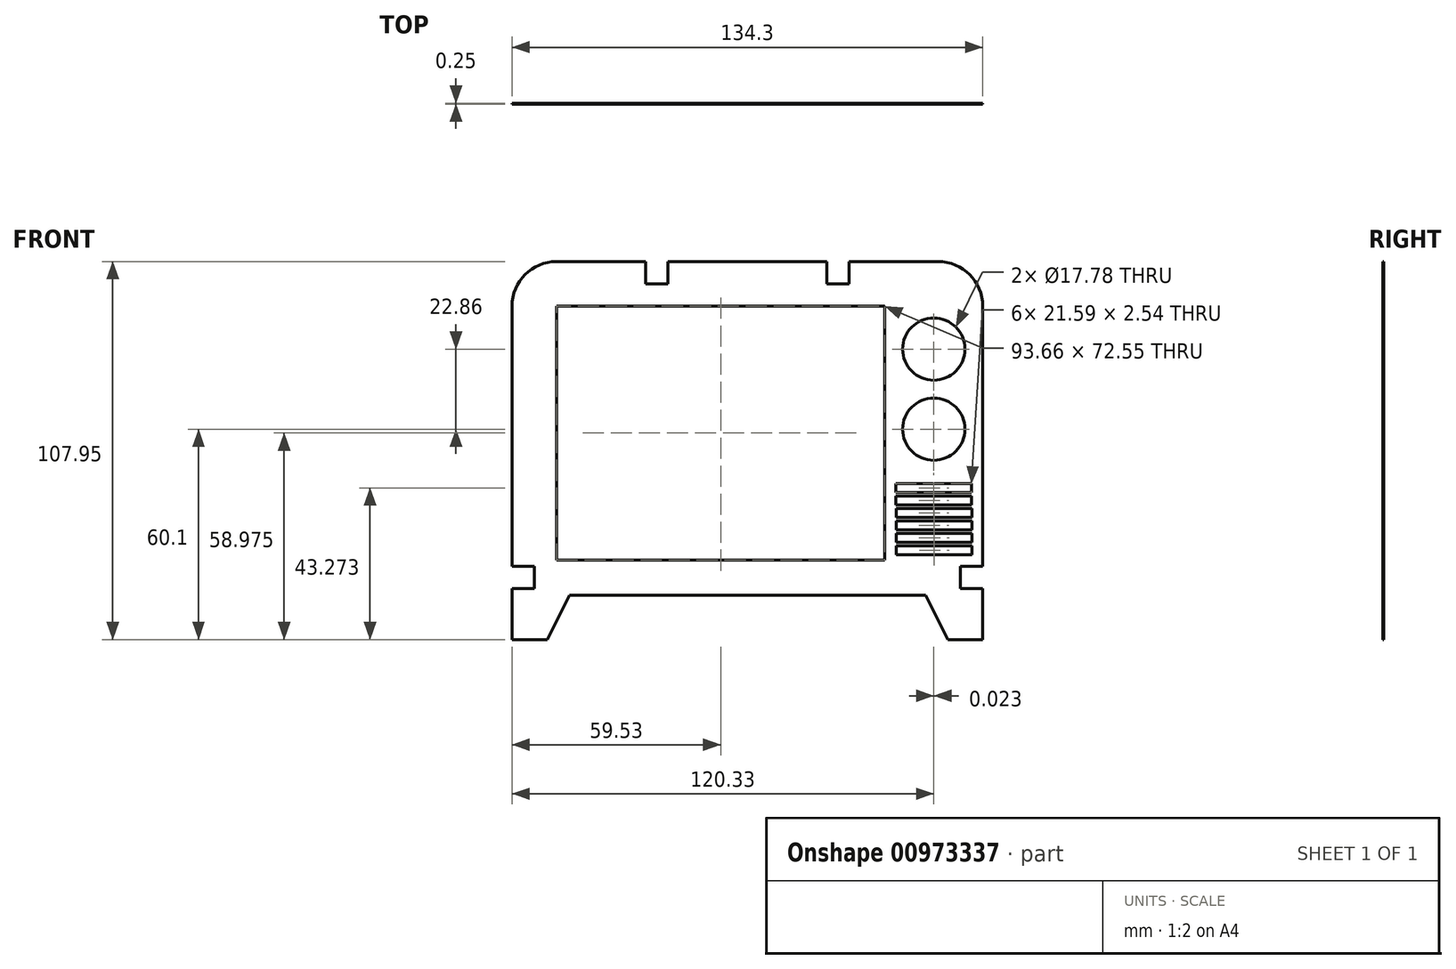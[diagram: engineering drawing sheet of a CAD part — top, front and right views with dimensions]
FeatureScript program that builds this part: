
annotation { "Feature Type Name" : "Feature", "Feature Type Description" : "" }
export const myFeature = defineFeature(function(context is Context, id is Id, definition is map)
    precondition{}
    {
        {
            assignVariable(context, id + "F0", {"name" : "Thick", "anyValue" : 0.25});
        }
        {
            var Q0;
            Q0=qCreatedBy(makeId("Front.planeOp"),FACE);
            var sketch = newSketch(context, id + "F1", { "sketchPlane" : qUnion([Q0])});
            skLineSegment(sketch, "E0", {"start": v(0, 0) * mm, "end": v(-50.8, 0) * mm});
            skLineSegment(sketch, "E1", {"start": v(-50.8, 0) * mm, "end": v(-57.15, -12.7) * mm});
            skLineSegment(sketch, "E2", {"start": v(-57.15, -12.7) * mm, "end": v(-67.15, -12.7) * mm});
            skLineSegment(sketch, "E3", {"start": v(0, 0) * mm, "end": v(0, 95.25) * mm, "construction": true});
            skLineSegment(sketch, "E4", {"start": v(0, 0) * mm, "end": v(-57.15, 0) * mm, "construction": true});
            skLineSegment(sketch, "E5", {"start": v(-57.15, 0) * mm, "end": v(-57.15, -12.7) * mm, "construction": true});
            skLineSegment(sketch, "E6.MirrorCS", {"start": v(0, 0) * mm, "end": v(50.8, 0) * mm});
            skLineSegment(sketch, "E7.MirrorCS", {"start": v(0, 0) * mm, "end": v(57.15, 0) * mm, "construction": true});
            skLineSegment(sketch, "E8.MirrorCS", {"start": v(57.15, 0) * mm, "end": v(57.15, -12.7) * mm, "construction": true});
            skLineSegment(sketch, "E9.MirrorCS", {"start": v(57.15, -12.7) * mm, "end": v(67.15, -12.7) * mm});
            skLineSegment(sketch, "E10.MirrorCS", {"start": v(50.8, 0) * mm, "end": v(57.15, -12.7) * mm});
            skPoint(sketch, "E11.visualSharp", {"position": v(-67.15, 95.25) * mm});
            skPoint(sketch, "E12.visualSharp", {"position": v(67.15, 95.25) * mm});
            skArc(sketch, "E12.filletArc", {"start": v(67.15, 82.55) * mm, "mid": v(63.43, 91.53) * mm, "end": v(54.45, 95.25) * mm});
            skLineSegment(sketch, "E13", {"start": v(-54.45, 82.55) * mm, "end": v(-54.45, 10) * mm});
            skLineSegment(sketch, "E14", {"start": v(-54.45, 10) * mm, "end": v(0, 10) * mm});
            skLineSegment(sketch, "E15", {"start": v(-54.45, 82.55) * mm, "end": v(0, 82.55) * mm});
            skLineSegment(sketch, "E16", {"start": v(0, 82.55) * mm, "end": v(39.2, 82.55) * mm});
            skLineSegment(sketch, "E17", {"start": v(0, 10) * mm, "end": v(39.21, 10) * mm});
            skLineSegment(sketch, "E18", {"start": v(39.2, 82.55) * mm, "end": v(39.21, 10) * mm});
            skLineSegment(sketch, "E19", {"start": v(67.15, 0) * mm, "end": v(53.18, 0) * mm, "construction": true});
            skLineSegment(sketch, "E20", {"start": v(53.18, -0.82) * mm, "end": v(53.18, 99.14) * mm, "construction": true});
            skLineSegment(sketch, "E21", {"start": v(84.24, 82.55) * mm, "end": v(84.24, 10) * mm, "construction": true});
            skCircle(sketch, "E22", {"center": v(53.18, 70.26) * mm, "radius": 8.9 * mm, "construction": true});
            skCircle(sketch, "E23.1.0.0", {"center": v(53.18, 47.4) * mm, "radius": 8.9 * mm, "construction": true});
            skLineSegment(sketch, "E23.direction1", {"start": v(53.18, 70.26) * mm, "end": v(53.18, 47.4) * mm, "construction": true});
            skLineSegment(sketch, "E24", {"start": v(63.18, 84.23) * mm, "end": v(63.18, 33.43) * mm, "construction": true});
            skLineSegment(sketch, "E25", {"start": v(63.18, 84.23) * mm, "end": v(36.84, 84.23) * mm, "construction": true});
            skLineSegment(sketch, "E26", {"start": v(63.18, 33.43) * mm, "end": v(34.94, 33.43) * mm, "construction": true});
            skLineSegment(sketch, "E27", {"start": v(63.18, 58.83) * mm, "end": v(36.84, 58.83) * mm, "construction": true});
            skLineSegment(sketch, "E28", {"start": v(53.18, 47.4) * mm, "end": v(53.18, 58.83) * mm, "construction": true});
            skLineSegment(sketch, "E29", {"start": v(53.18, 79.15) * mm, "end": v(53.18, 84.23) * mm, "construction": true});
            skLineSegment(sketch, "E30", {"start": v(53.18, 38.51) * mm, "end": v(53.18, 33.43) * mm, "construction": true});
            skLineSegment(sketch, "E31", {"start": v(53.18, 61.37) * mm, "end": v(53.18, 56.3) * mm, "construction": true});
            skCircle(sketch, "E32", {"center": v(53.18, 70.26) * mm, "radius": 8.9 * mm});
            skCircle(sketch, "E33", {"center": v(53.18, 47.4) * mm, "radius": 8.9 * mm});
            skLineSegment(sketch, "E34.bottom", {"start": v(42.38, 31.84) * mm, "end": v(63.98, 31.84) * mm});
            skLineSegment(sketch, "E34.top", {"start": v(42.38, 29.3) * mm, "end": v(63.98, 29.3) * mm});
            skLineSegment(sketch, "E34.left", {"start": v(42.38, 31.84) * mm, "end": v(42.38, 29.3) * mm});
            skLineSegment(sketch, "E34.right", {"start": v(63.98, 31.84) * mm, "end": v(63.98, 29.3) * mm});
            skLineSegment(sketch, "E35.1.0.0", {"start": v(42.4, 28.29) * mm, "end": v(42.4, 25.75) * mm});
            skLineSegment(sketch, "E35.1.0.1", {"start": v(42.4, 28.29) * mm, "end": v(64, 28.29) * mm});
            skLineSegment(sketch, "E35.1.0.2", {"start": v(42.4, 25.75) * mm, "end": v(64, 25.75) * mm});
            skLineSegment(sketch, "E35.1.0.3", {"start": v(64, 28.29) * mm, "end": v(64, 25.75) * mm});
            skLineSegment(sketch, "E35.2.0.0", {"start": v(42.43, 24.73) * mm, "end": v(42.43, 22.2) * mm});
            skLineSegment(sketch, "E35.2.0.1", {"start": v(42.43, 24.73) * mm, "end": v(64.02, 24.73) * mm});
            skLineSegment(sketch, "E35.2.0.2", {"start": v(42.43, 22.2) * mm, "end": v(64.02, 22.2) * mm});
            skLineSegment(sketch, "E35.2.0.3", {"start": v(64.02, 24.73) * mm, "end": v(64.02, 22.2) * mm});
            skLineSegment(sketch, "E35.direction1", {"start": v(42.38, 29.3) * mm, "end": v(42.4, 25.75) * mm, "construction": true});
            skLineSegment(sketch, "E36.0.3.0", {"start": v(42.45, 21.18) * mm, "end": v(42.45, 18.64) * mm});
            skLineSegment(sketch, "E36.3.3.0", {"start": v(42.45, 21.18) * mm, "end": v(64.04, 21.18) * mm});
            skLineSegment(sketch, "E36.6.3.0", {"start": v(42.45, 18.64) * mm, "end": v(64.04, 18.64) * mm});
            skLineSegment(sketch, "E36.9.3.0", {"start": v(64.04, 21.18) * mm, "end": v(64.04, 18.64) * mm});
            skLineSegment(sketch, "E36.0.4.0", {"start": v(42.48, 17.62) * mm, "end": v(42.48, 15.08) * mm});
            skLineSegment(sketch, "E36.3.4.0", {"start": v(42.48, 17.62) * mm, "end": v(64.07, 17.62) * mm});
            skLineSegment(sketch, "E36.6.4.0", {"start": v(42.48, 15.08) * mm, "end": v(64.07, 15.08) * mm});
            skLineSegment(sketch, "E36.9.4.0", {"start": v(64.07, 17.62) * mm, "end": v(64.07, 15.08) * mm});
            skLineSegment(sketch, "E37", {"start": v(-67.15, 70.65) * mm, "end": v(-67.15, 8.17) * mm});
            skLineSegment(sketch, "E38", {"start": v(-67.15, 8.17) * mm, "end": v(-60.8, 8.17) * mm});
            skLineSegment(sketch, "E39", {"start": v(-60.8, 8.17) * mm, "end": v(-60.8, 1.82) * mm});
            skLineSegment(sketch, "E40", {"start": v(-60.8, 1.82) * mm, "end": v(-67.15, 1.82) * mm});
            skLineSegment(sketch, "E41", {"start": v(-67.15, 1.82) * mm, "end": v(-67.15, -12.7) * mm});
            skLineSegment(sketch, "E42", {"start": v(-50.8, 0) * mm, "end": v(-50.8, 10) * mm, "construction": true});
            skPoint(sketch, "E43", {"position": v(-50.8, 5) * mm});
            skPoint(sketch, "E44", {"position": v(-60.8, 5) * mm});
            skLineSegment(sketch, "E45", {"start": v(-67.15, 70.65) * mm, "end": v(-67.15, 82.55) * mm});
            skLineSegment(sketch, "E46", {"start": v(-48.12, 95.25) * mm, "end": v(-54.45, 95.25) * mm});
            skArc(sketch, "E47.filletArc", {"start": v(-54.45, 95.25) * mm, "mid": v(-63.43, 91.53) * mm, "end": v(-67.15, 82.55) * mm});
            skLineSegment(sketch, "E48.MirrorCS", {"start": v(67.15, 8.17) * mm, "end": v(60.8, 8.17) * mm});
            skLineSegment(sketch, "E49.MirrorCS", {"start": v(60.8, 1.82) * mm, "end": v(67.15, 1.82) * mm});
            skLineSegment(sketch, "E50.MirrorCS", {"start": v(67.15, 1.82) * mm, "end": v(67.15, -12.7) * mm});
            skLineSegment(sketch, "E51.MirrorCS", {"start": v(60.8, 8.17) * mm, "end": v(60.8, 1.82) * mm});
            skPoint(sketch, "E52.MirrorP", {"position": v(60.8, 5) * mm});
            skLineSegment(sketch, "E53", {"start": v(67.15, 8.17) * mm, "end": v(67.15, 82.55) * mm});
            skLineSegment(sketch, "E54.0.5.0", {"start": v(42.5, 14.06) * mm, "end": v(42.5, 11.52) * mm});
            skLineSegment(sketch, "E54.3.5.0", {"start": v(42.5, 14.06) * mm, "end": v(64.09, 14.06) * mm});
            skLineSegment(sketch, "E54.6.5.0", {"start": v(42.5, 11.52) * mm, "end": v(64.09, 11.52) * mm});
            skLineSegment(sketch, "E54.9.5.0", {"start": v(64.09, 14.06) * mm, "end": v(64.09, 11.52) * mm});
            skLineSegment(sketch, "E55", {"start": v(-54.45, 95.25) * mm, "end": v(-29.05, 95.25) * mm, "construction": true});
            skLineSegment(sketch, "E56", {"start": v(-48.12, 95.25) * mm, "end": v(-29.05, 95.25) * mm});
            skLineSegment(sketch, "E57", {"start": v(-29.05, 88.9) * mm, "end": v(-22.7, 88.9) * mm});
            skLineSegment(sketch, "E58", {"start": v(-22.7, 88.9) * mm, "end": v(-22.7, 95.25) * mm});
            skLineSegment(sketch, "E59", {"start": v(-22.7, 95.25) * mm, "end": v(0, 95.25) * mm});
            skLineSegment(sketch, "E60", {"start": v(-29.05, 88.9) * mm, "end": v(-29.05, 95.25) * mm});
            skLineSegment(sketch, "E61.MirrorCS", {"start": v(48.12, 95.25) * mm, "end": v(54.45, 95.25) * mm});
            skLineSegment(sketch, "E62.MirrorCS", {"start": v(48.12, 95.25) * mm, "end": v(29.05, 95.25) * mm});
            skLineSegment(sketch, "E63.MirrorCS", {"start": v(22.7, 95.25) * mm, "end": v(0, 95.25) * mm});
            skLineSegment(sketch, "E64.MirrorCS", {"start": v(29.05, 88.9) * mm, "end": v(29.05, 95.25) * mm});
            skLineSegment(sketch, "E65.MirrorCS", {"start": v(22.7, 88.9) * mm, "end": v(22.7, 95.25) * mm});
            skLineSegment(sketch, "E66.MirrorCS", {"start": v(29.05, 88.9) * mm, "end": v(22.7, 88.9) * mm});
            skSolve(sketch);
        }
        {
            var Q0;
            Q0 = qSketchRegion(id + "F1", true);
            extrude(context, id + "F2", {"entities" : qUnion([Q0]), "depth" : (getVariable(context, 'Thick')) * mm, "offsetDistance" : 25.4 * mm});
        }
    });
